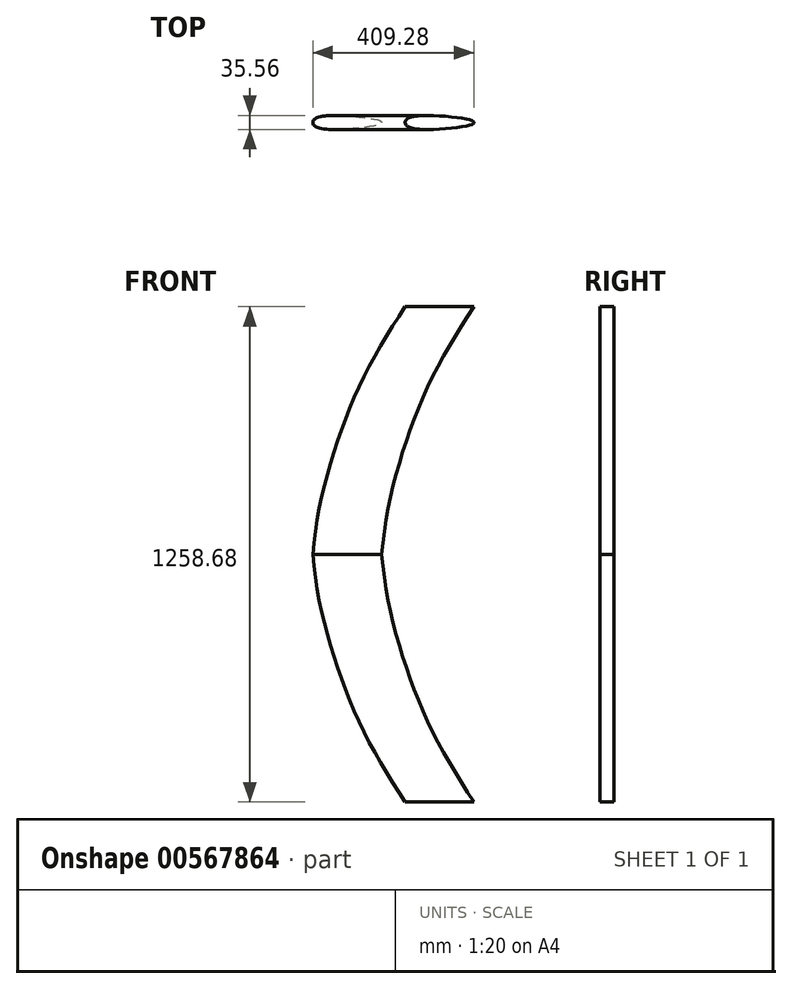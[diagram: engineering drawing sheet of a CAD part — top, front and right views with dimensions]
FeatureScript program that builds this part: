
annotation { "Feature Type Name" : "Feature", "Feature Type Description" : "" }
export const myFeature = defineFeature(function(context is Context, id is Id, definition is map)
    precondition{}
    {
        {
            var Q0;
            Q0=qCreatedBy(makeId("Top.planeOp"),FACE);
            var sketch = newSketch(context, id + "F0", { "sketchPlane" : qUnion([Q0])});
            skFitSpline(sketch, "E0", {"points": [v(0, 15) * mm, v(150, 5) * mm, v(155, 0) * mm, v(150, -5) * mm, v(0, -15) * mm, v(-19.67, 0) * mm, v(0, 15) * mm]});
            skSolve(sketch);
        }
        {
            var Q0;
            Q0=qCreatedBy(makeId("Front.planeOp"),FACE);
            var sketch = newSketch(context, id + "F1", { "sketchPlane" : qUnion([Q0])});
            skFitSpline(sketch, "E1", {"points": [v(0, 0) * mm, v(22.73, 147) * mm, v(116.44, 423.23) * mm, v(234.6, 629.34) * mm], "startDerivative": vector(52.52, 489.68) * mm, "endDerivative": vector(355.47, 551.62) * mm});
            skFitSpline(sketch, "E2.MirrorCS", {"points": [v(0, 0) * mm, v(22.73, -147) * mm, v(116.44, -423.23) * mm, v(234.6, -629.34) * mm], "startDerivative": vector(52.52, -489.68) * mm, "endDerivative": vector(355.47, -551.62) * mm});
            skSolve(sketch);
        }
        {
            var Q0;
            Q0=makeQuery(id+"F0.imprint","IMPRINT",FACE,{"disambiguationData":[TD([[makeQuery(id+"F0.imprint","IMPRINT",EDGE,{"derivedFrom":sQuery(id+"F0.wireOp",EDGE,"E0")}),-1.0]])]});
            var Q1;
            Q1=sQuery(id+"F1.wireOp",EDGE,"E2.MirrorCS");
            sweep(context, id + "F2", {"profiles" : qUnion([Q0]), "path" : qUnion([Q1]), "keepProfileOrientation" : true});
        }
        {
            var Q0;
            Q0=makeQuery(id+"F2.opSweep","CAP_FACE",FACE,{"disambiguationData":[OSD([sQuery(id+"F0.wireOp",EDGE,"E0"),sQuery(id+"F1.wireOp",VERTEX,"E2.MirrorCS.start")])],"isStart":true});
            var Q1;
            Q1=sQuery(id+"F1.wireOp",EDGE,"E1");
            sweep(context, id + "F3", {"operationType" : NewBodyOperationType.ADD, "profiles" : qUnion([Q0]), "path" : qUnion([Q1]), "keepProfileOrientation" : true});
        }
    });
